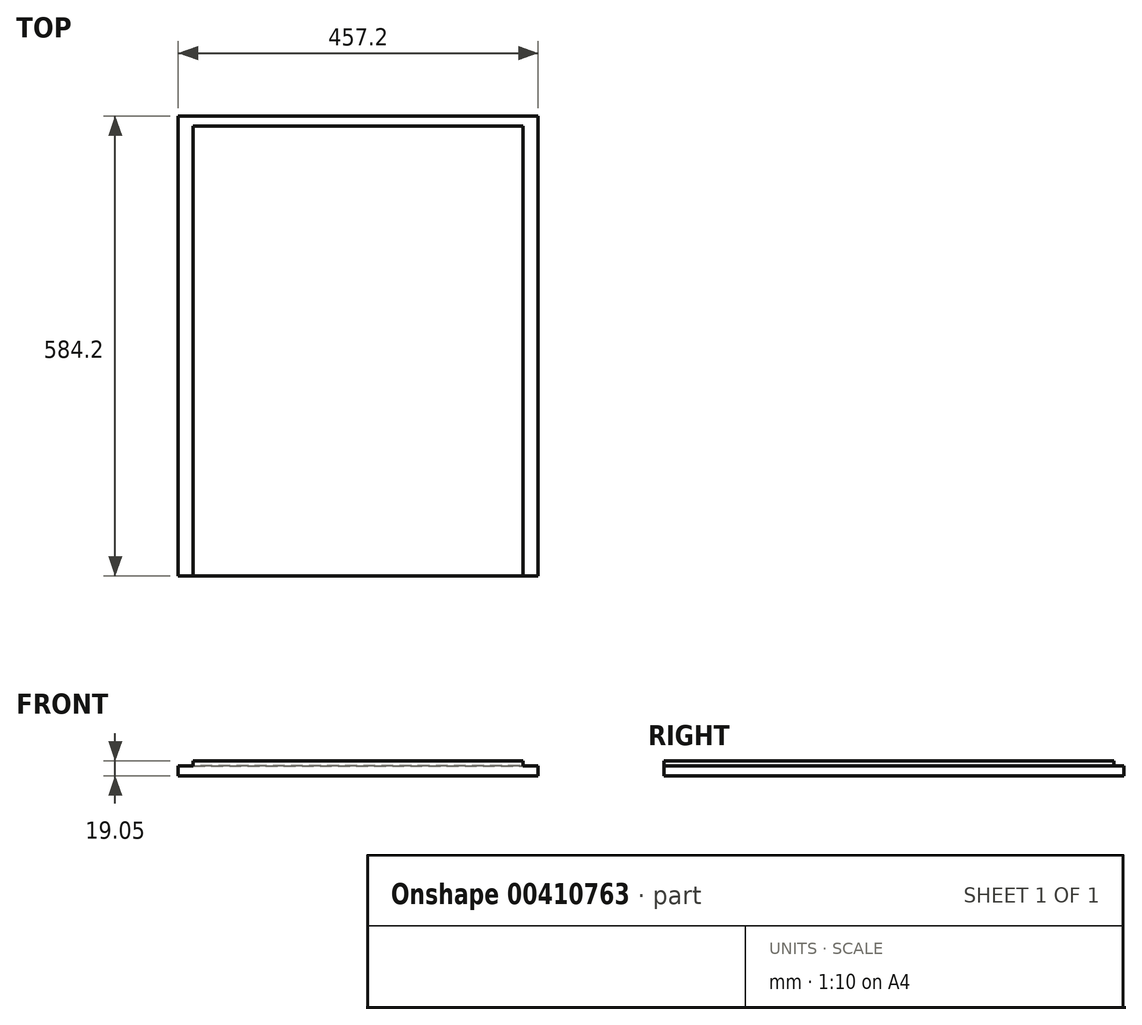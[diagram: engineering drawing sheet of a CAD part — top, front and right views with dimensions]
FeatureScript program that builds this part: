
annotation { "Feature Type Name" : "Feature", "Feature Type Description" : "" }
export const myFeature = defineFeature(function(context is Context, id is Id, definition is map)
    precondition{}
    {
        {
            var Q0;
            Q0=qCreatedBy(makeId("Top.planeOp"),FACE);
            var sketch = newSketch(context, id + "F0", { "sketchPlane" : qUnion([Q0])});
            skLineSegment(sketch, "E0", {"start": v(228.6, -304.8) * mm, "end": v(228.6, 279.4) * mm});
            skLineSegment(sketch, "E1", {"start": v(228.6, 279.4) * mm, "end": v(-228.6, 279.4) * mm});
            skLineSegment(sketch, "E2", {"start": v(-228.6, 279.4) * mm, "end": v(-228.6, -304.8) * mm});
            skLineSegment(sketch, "E3", {"start": v(-228.6, -304.8) * mm, "end": v(228.6, -304.8) * mm});
            skSolve(sketch);
        }
        {
            var Q0;
            Q0 = qSketchRegion(id + "F0", true);
            extrude(context, id + "F1", {"entities" : qUnion([Q0]), "depth" : 19.05 * mm});
        }
        {
            var Q0;
            Q0=makeQuery(id+"F1.opExtrude","CAP_FACE",FACE,{"disambiguationData":[OSD([sQuery(id+"F0.wireOp",EDGE,"E0"),sQuery(id+"F0.wireOp",EDGE,"E1"),sQuery(id+"F0.wireOp",EDGE,"E2"),sQuery(id+"F0.wireOp",EDGE,"E3")])],"isStart":false});
            var sketch = newSketch(context, id + "F2", { "sketchPlane" : qUnion([Q0])});
            skLineSegment(sketch, "E4.bottom", {"start": v(228.6, -304.8) * mm, "end": v(209.55, -304.8) * mm});
            skLineSegment(sketch, "E4.top", {"start": v(228.6, 279.4) * mm, "end": v(209.55, 279.4) * mm});
            skLineSegment(sketch, "E4.left", {"start": v(228.6, -304.8) * mm, "end": v(228.6, 279.4) * mm});
            skLineSegment(sketch, "E4.right", {"start": v(209.55, -304.8) * mm, "end": v(209.55, 279.4) * mm});
            skLineSegment(sketch, "E5.bottom", {"start": v(-228.6, -304.8) * mm, "end": v(-209.55, -304.8) * mm});
            skLineSegment(sketch, "E5.top", {"start": v(-228.6, 279.4) * mm, "end": v(-209.55, 279.4) * mm});
            skLineSegment(sketch, "E5.left", {"start": v(-228.6, -304.8) * mm, "end": v(-228.6, 279.4) * mm});
            skLineSegment(sketch, "E5.right", {"start": v(-209.55, -304.8) * mm, "end": v(-209.55, 279.4) * mm});
            skSolve(sketch);
        }
        {
            var Q0;
            Q0 = qSketchRegion(id + "F2", true);
            extrude(context, id + "F3", {"entities" : qUnion([Q0]), "operationType" : NewBodyOperationType.REMOVE, "oppositeDirection" : true, "depth" : 6.35 * mm});
        }
        {
            var Q0;
            Q0=makeQuery(id+"F1.opExtrude","CAP_FACE",FACE,{"disambiguationData":[OSD([sQuery(id+"F0.wireOp",EDGE,"E0"),sQuery(id+"F0.wireOp",EDGE,"E1"),sQuery(id+"F0.wireOp",EDGE,"E2"),sQuery(id+"F0.wireOp",EDGE,"E3")])],"isStart":false});
            var sketch = newSketch(context, id + "F4", { "sketchPlane" : qUnion([Q0])});
            skLineSegment(sketch, "E6.bottom", {"start": v(-209.55, 279.4) * mm, "end": v(209.55, 279.4) * mm});
            skLineSegment(sketch, "E6.top", {"start": v(-209.55, 266.7) * mm, "end": v(209.55, 266.7) * mm});
            skLineSegment(sketch, "E6.left", {"start": v(-209.55, 279.4) * mm, "end": v(-209.55, 266.7) * mm});
            skLineSegment(sketch, "E6.right", {"start": v(209.55, 279.4) * mm, "end": v(209.55, 266.7) * mm});
            skSolve(sketch);
        }
        {
            var Q0;
            Q0 = qSketchRegion(id + "F4", true);
            extrude(context, id + "F5", {"entities" : qUnion([Q0]), "operationType" : NewBodyOperationType.REMOVE, "oppositeDirection" : true, "depth" : 6.35 * mm});
        }
    });
